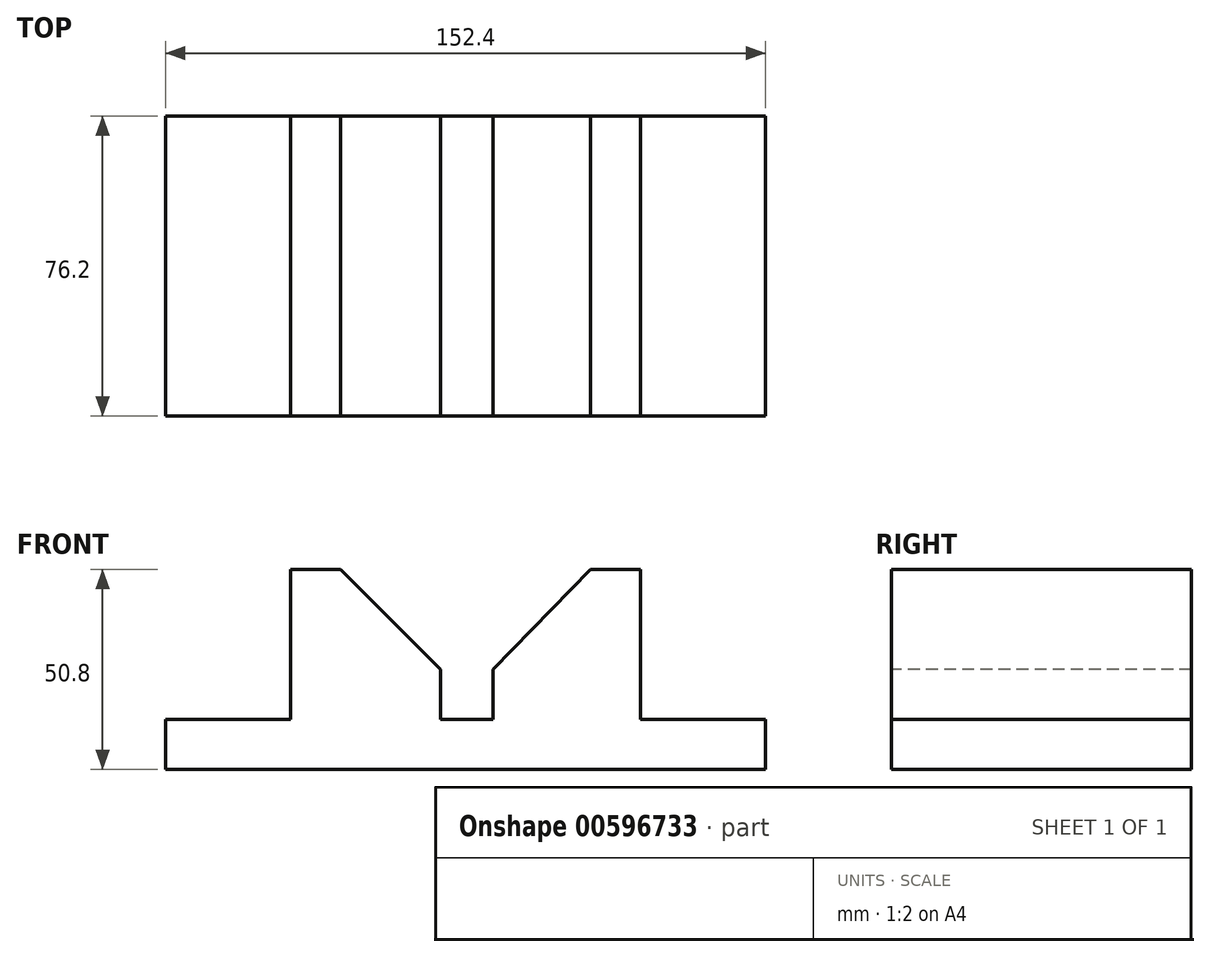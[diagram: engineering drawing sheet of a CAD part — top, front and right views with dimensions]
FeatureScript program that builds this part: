
annotation { "Feature Type Name" : "Feature", "Feature Type Description" : "" }
export const myFeature = defineFeature(function(context is Context, id is Id, definition is map)
    precondition{}
    {
        {
            var Q0;
            Q0=qCreatedBy(makeId("Front.planeOp"),FACE);
            var sketch = newSketch(context, id + "F0", { "sketchPlane" : qUnion([Q0])});
            skLineSegment(sketch, "E0.bottom", {"start": v(0, 0) * mm, "end": v(-152.4, 0) * mm});
            skLineSegment(sketch, "E0.top", {"start": v(0, 50.8) * mm, "end": v(-152.4, 50.8) * mm});
            skLineSegment(sketch, "E0.left", {"start": v(0, 0) * mm, "end": v(0, 50.8) * mm});
            skLineSegment(sketch, "E0.right", {"start": v(-152.4, 0) * mm, "end": v(-152.4, 50.8) * mm});
            skSolve(sketch);
        }
        {
            var Q0;
            Q0=makeQuery(id+"F0.imprint","IMPRINT",FACE,{"disambiguationData":[TD([[makeQuery(id+"F0.imprint","IMPRINT",EDGE,{"derivedFrom":sQuery(id+"F0.wireOp",EDGE,"E0.bottom")}),-1.0]])]});
            extrude(context, id + "F1", {"entities" : qUnion([Q0]), "depth" : 76.2 * mm, "offsetDistance" : 25.4 * mm});
        }
        {
            var Q0;
            Q0=makeQuery(id+"F1.opExtrude","CAP_FACE",FACE,{"disambiguationData":[OSD([sQuery(id+"F0.wireOp",EDGE,"E0.bottom"),sQuery(id+"F0.wireOp",EDGE,"E0.top"),sQuery(id+"F0.wireOp",EDGE,"E0.left"),sQuery(id+"F0.wireOp",EDGE,"E0.right")])],"isStart":false});
            var sketch = newSketch(context, id + "F2", { "sketchPlane" : qUnion([Q0])});
            skLineSegment(sketch, "E1", {"start": v(-152.4, 0) * mm, "end": v(-152.4, 12.7) * mm});
            skLineSegment(sketch, "E2", {"start": v(-152.4, 12.7) * mm, "end": v(-120.65, 12.7) * mm});
            skLineSegment(sketch, "E3", {"start": v(-120.65, 12.7) * mm, "end": v(-120.65, 50.8) * mm});
            skLineSegment(sketch, "E4", {"start": v(-120.65, 50.8) * mm, "end": v(-107.95, 50.8) * mm});
            skLineSegment(sketch, "E5", {"start": v(-82.55, 12.7) * mm, "end": v(-82.55, 25.4) * mm});
            skLineSegment(sketch, "E6", {"start": v(-107.95, 50.8) * mm, "end": v(-82.55, 25.4) * mm});
            skLineSegment(sketch, "E7", {"start": v(-120.65, 12.7) * mm, "end": v(-82.55, 12.7) * mm});
            skLineSegment(sketch, "E8", {"start": v(-82.55, 12.7) * mm, "end": v(-69.21, 12.7) * mm});
            skLineSegment(sketch, "E9", {"start": v(-69.21, 12.7) * mm, "end": v(-69.21, 25.4) * mm});
            skLineSegment(sketch, "E10", {"start": v(0, 0) * mm, "end": v(0, 12.7) * mm});
            skLineSegment(sketch, "E11", {"start": v(0, 12.7) * mm, "end": v(-31.75, 12.7) * mm});
            skLineSegment(sketch, "E12", {"start": v(-31.75, 12.7) * mm, "end": v(-31.75, 50.8) * mm});
            skLineSegment(sketch, "E13", {"start": v(-31.75, 50.8) * mm, "end": v(-44.45, 50.8) * mm});
            skLineSegment(sketch, "E14", {"start": v(-44.45, 50.8) * mm, "end": v(-69.21, 25.4) * mm});
            skLineSegment(sketch, "E15", {"start": v(-69.21, 12.7) * mm, "end": v(-31.75, 12.7) * mm});
            skSolve(sketch);
        }
        {
            var Q0;
            {var subQ0=sQuery(id+"F2.wireOp",EDGE,"E2");Q0=makeQuery(id+"F2.imprint","IMPRINT",FACE,{"disambiguationData":[TD([[makeQuery(id+"F2.imprint","IMPRINT",EDGE,{"derivedFrom":subQ0}),1.0]])]});}
            var Q1;
            Q1=makeQuery(id+"F2.imprint","IMPRINT",FACE,{"disambiguationData":[TD([[makeQuery(id+"F2.imprint","IMPRINT",EDGE,{"derivedFrom":sQuery(id+"F2.wireOp",EDGE,"E5")}),-1.0]])]});
            var Q2;
            {var subQ0=sQuery(id+"F2.wireOp",EDGE,"E11");Q2=makeQuery(id+"F2.imprint","IMPRINT",FACE,{"disambiguationData":[TD([[makeQuery(id+"F2.imprint","IMPRINT",EDGE,{"derivedFrom":subQ0}),-1.0]])]});}
            extrude(context, id + "F3", {"entities" : qUnion([Q0, Q1, Q2]), "operationType" : NewBodyOperationType.REMOVE, "oppositeDirection" : true, "depth" : 131.83 * mm, "offsetDistance" : 25.4 * mm});
        }
    });
